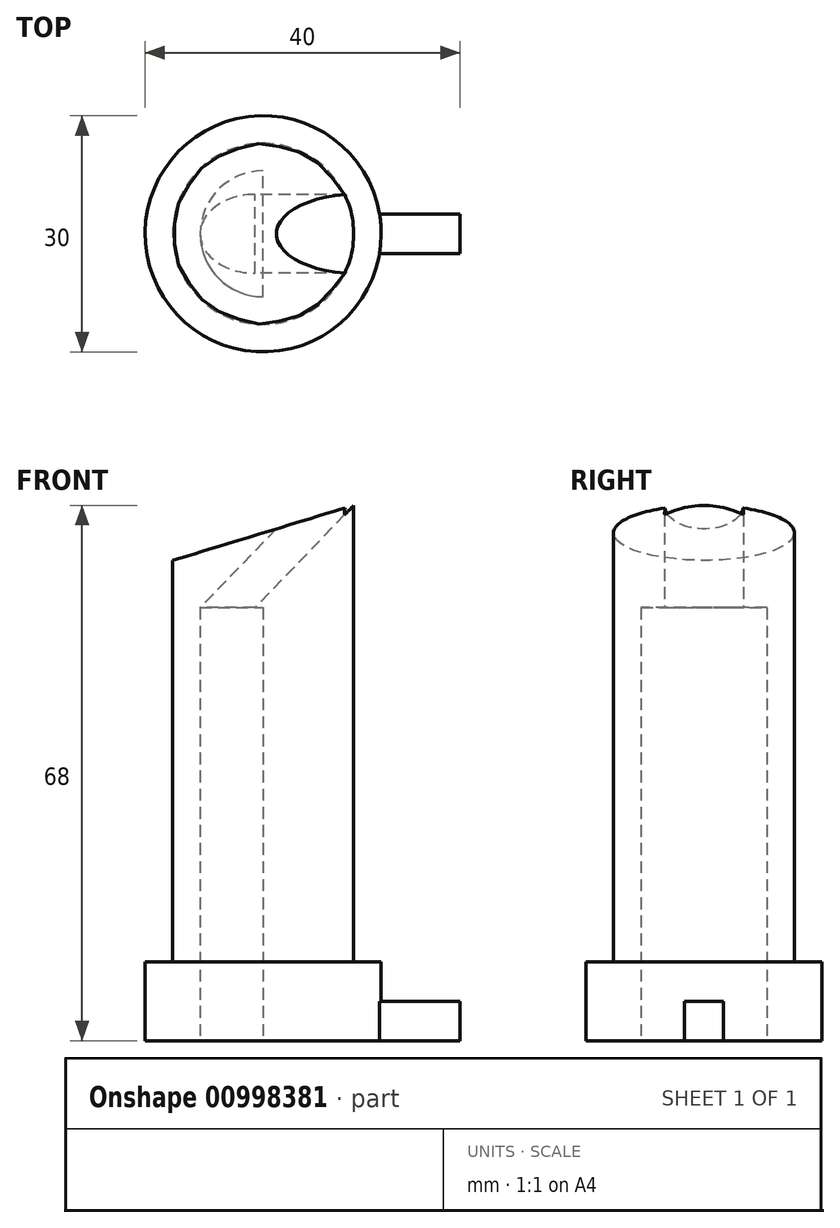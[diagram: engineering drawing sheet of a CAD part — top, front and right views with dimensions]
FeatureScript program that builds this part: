
annotation { "Feature Type Name" : "Feature", "Feature Type Description" : "" }
export const myFeature = defineFeature(function(context is Context, id is Id, definition is map)
    precondition{}
    {
        {
            var Q0;
            Q0=qCreatedBy(makeId("Top.planeOp"),FACE);
            var sketch = newSketch(context, id + "F0", { "sketchPlane" : qUnion([Q0])});
            skCircle(sketch, "E0", {"center": v(0, 0) * mm, "radius": 15 * mm});
            skCircle(sketch, "E1", {"center": v(0, 0) * mm, "radius": 11.5 * mm});
            skSolve(sketch);
        }
        {
            var Q0;
            Q0 = qSketchRegion(id + "F0", true);
            extrude(context, id + "F1", {"entities" : qUnion([Q0]), "depth" : 10 * mm, "offsetDistance" : 25 * mm});
        }
        {
            var Q0;
            Q0=makeQuery(id+"F0.imprint","IMPRINT",FACE,{"disambiguationData":[TD([[makeQuery(id+"F0.imprint","IMPRINT",EDGE,{"derivedFrom":sQuery(id+"F0.wireOp",EDGE,"E1")}),1.0]])]});
            extrude(context, id + "F2", {"entities" : qUnion([Q0]), "operationType" : NewBodyOperationType.ADD, "depth" : 68 * mm, "offsetDistance" : 25 * mm});
        }
        {
            var Q0;
            Q0=qCreatedBy(makeId("Top.planeOp"),FACE);
            var sketch = newSketch(context, id + "F3", { "sketchPlane" : qUnion([Q0])});
            skCircle(sketch, "E2.0", {"center": v(0, 0) * mm, "radius": 15 * mm});
            skLineSegment(sketch, "E3", {"start": v(0, 0) * mm, "end": v(25, 0) * mm});
            skLineSegment(sketch, "E4", {"start": v(14.8, -2.5) * mm, "end": v(25, -2.5) * mm});
            skLineSegment(sketch, "E5", {"start": v(25, -2.5) * mm, "end": v(25, 2.5) * mm});
            skLineSegment(sketch, "E6", {"start": v(25, 2.5) * mm, "end": v(14.8, 2.5) * mm});
            skSolve(sketch);
        }
        {
            var Q0;
            {var subQ0=sQuery(id+"F3.wireOp",EDGE,"E4");Q0=makeQuery(id+"F3.imprint","IMPRINT",FACE,{"disambiguationData":[TD([[makeQuery(id+"F3.imprint","IMPRINT",EDGE,{"derivedFrom":subQ0}),1.0]])]});}
            var Q1;
            {var subQ0=sQuery(id+"F3.wireOp",EDGE,"E6");Q1=makeQuery(id+"F3.imprint","IMPRINT",FACE,{"disambiguationData":[TD([[makeQuery(id+"F3.imprint","IMPRINT",EDGE,{"derivedFrom":subQ0}),1.0]])]});}
            extrude(context, id + "F4", {"entities" : qUnion([Q0, Q1]), "operationType" : NewBodyOperationType.ADD, "depth" : 5 * mm, "offsetDistance" : 25 * mm});
        }
        {
            var Q0;
            Q0=qCreatedBy(makeId("Front.planeOp"),FACE);
            var sketch = newSketch(context, id + "F5", { "sketchPlane" : qUnion([Q0])});
            skLineSegment(sketch, "E7.0", {"start": v(-11.5, 10) * mm, "end": v(11.5, 10) * mm});
            skLineSegment(sketch, "E8.0", {"start": v(-11.5, 68) * mm, "end": v(11.5, 68) * mm});
            skLineSegment(sketch, "E9", {"start": v(11.5, 68) * mm, "end": v(11.5, 10) * mm});
            skLineSegment(sketch, "E10", {"start": v(11.5, 68) * mm, "end": v(-11.5, 61) * mm});
            skLineSegment(sketch, "E11", {"start": v(-11.5, 61) * mm, "end": v(-11.5, 10) * mm});
            skLineSegment(sketch, "E12", {"start": v(-11.5, 61) * mm, "end": v(-11.5, 68) * mm});
            skSolve(sketch);
        }
        {
            var Q0;
            Q0=makeQuery(id+"F5.imprint","IMPRINT",FACE,{"disambiguationData":[TD([[makeQuery(id+"F5.imprint","IMPRINT",EDGE,{"derivedFrom":sQuery(id+"F5.wireOp",EDGE,"E8.0")}),-1.0]])]});
            extrude(context, id + "F6", {"entities" : qUnion([Q0]), "operationType" : NewBodyOperationType.REMOVE, "endBound" : BoundingType.SYMMETRIC, "oppositeDirection" : true, "depth" : 100 * mm, "offsetDistance" : 25 * mm});
        }
        {
            var Q0;
            Q0=qCreatedBy(makeId("Top.planeOp"),FACE);
            var sketch = newSketch(context, id + "F7", { "sketchPlane" : qUnion([Q0])});
            skCircle(sketch, "E13.0", {"center": v(0, 0) * mm, "radius": 11.5 * mm});
            skCircle(sketch, "E14", {"center": v(0, 0) * mm, "radius": 8 * mm});
            skLineSegment(sketch, "E15", {"start": v(0, -8) * mm, "end": v(0, 8) * mm});
            skSolve(sketch);
        }
        {
            var Q0;
            {var subQ0=sQuery(id+"F7.wireOp",EDGE,"E15");Q0=makeQuery(id+"F7.imprint","IMPRINT",FACE,{"disambiguationData":[TD([[makeQuery(id+"F7.imprint","IMPRINT",EDGE,{"derivedFrom":subQ0}),1.0]])]});}
            extrude(context, id + "F8", {"entities" : qUnion([Q0]), "operationType" : NewBodyOperationType.REMOVE, "depth" : 55 * mm, "offsetDistance" : 25 * mm});
        }
        {
            var Q0;
            Q0=qCreatedBy(makeId("Front.planeOp"),FACE);
            var sketch = newSketch(context, id + "F9", { "sketchPlane" : qUnion([Q0])});
            skLineSegment(sketch, "E16.0.0", {"start": v(0, 0) * mm, "end": v(-8, 0) * mm});
            skLineSegment(sketch, "E16.0.1", {"start": v(0, 0) * mm, "end": v(0, 55) * mm});
            skLineSegment(sketch, "E16.0.2", {"start": v(0, 55) * mm, "end": v(-8, 55) * mm});
            skLineSegment(sketch, "E16.0.3", {"start": v(0, 55) * mm, "end": v(0, 0) * mm});
            skLineSegment(sketch, "E17.0", {"start": v(11.5, 68) * mm, "end": v(-11.5, 61) * mm});
            skLineSegment(sketch, "E18", {"start": v(-8, 55) * mm, "end": v(1.66, 65) * mm});
            skLineSegment(sketch, "E19", {"start": v(11.5, 68) * mm, "end": v(-1.05, 55) * mm});
            skSolve(sketch);
        }
        {
            var Q0;
            Q0=sQuery(id+"F9.wireOp",VERTEX,"E16.0.2.end");
            var Q1;
            Q1=sQuery(id+"F9.wireOp",EDGE,"E18");
            cPlane(context, id + "F10", {"entities" : qUnion([Q0, Q1]), "cplaneType" : CPlaneType.LINE_POINT, "offset" : 25 * mm, "width" : 150 * mm, "height" : 150 * mm});
        }
        {
            var Q0;
            Q0=qCreatedBy(id+"F10.planeOp",FACE);
            var sketch = newSketch(context, id + "F11", { "sketchPlane" : qUnion([Q0])});
            skPoint(sketch, "E20.0", {"position": v(-38.96, 0) * mm});
            skPoint(sketch, "E21.0", {"position": v(-43.96, 0) * mm});
            skCircle(sketch, "E22", {"center": v(-38.96, 0) * mm, "radius": 5 * mm});
            skLineSegment(sketch, "E23", {"start": v(-38.96, 5) * mm, "end": v(-38.96, -5) * mm});
            skLineSegment(sketch, "E24", {"start": v(-43.96, 0) * mm, "end": v(-38.96, 0) * mm, "construction": true});
            skSolve(sketch);
        }
        {
            var Q0;
            {var subQ0=sQuery(id+"F11.wireOp",EDGE,"E23");Q0=makeQuery(id+"F11.imprint","IMPRINT",FACE,{"disambiguationData":[TD([[makeQuery(id+"F11.imprint","IMPRINT",EDGE,{"derivedFrom":subQ0}),-1.0]])]});}
            extrude(context, id + "F12", {"entities" : qUnion([Q0]), "operationType" : NewBodyOperationType.REMOVE, "depth" : 25 * mm, "offsetDistance" : 25 * mm});
        }
    });
